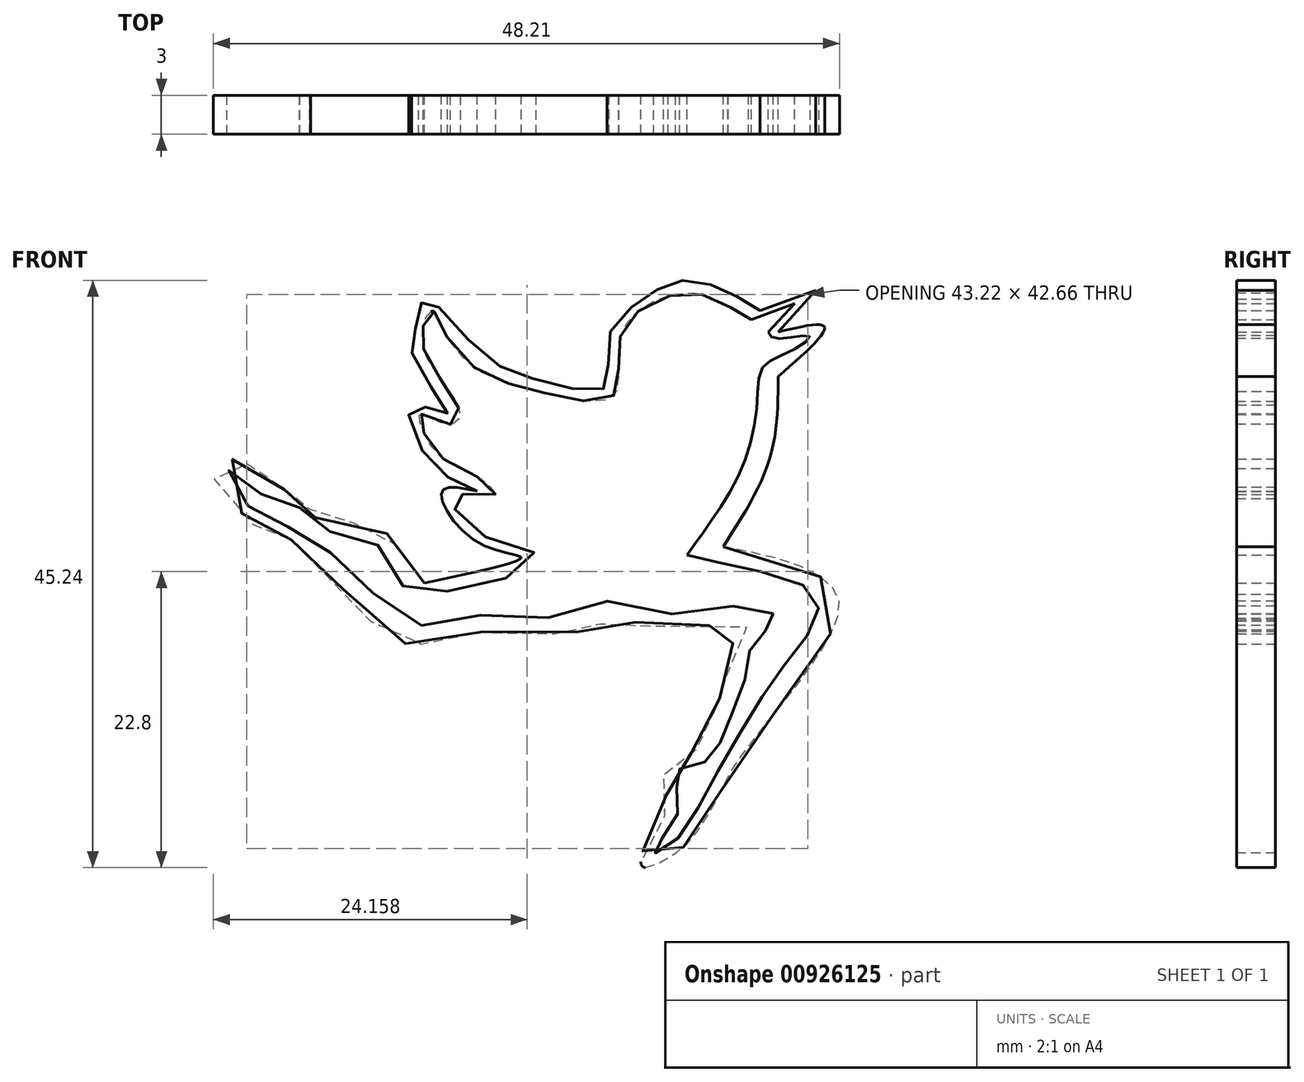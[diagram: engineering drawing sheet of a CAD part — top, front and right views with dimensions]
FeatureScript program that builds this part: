
annotation { "Feature Type Name" : "Feature", "Feature Type Description" : "" }
export const myFeature = defineFeature(function(context is Context, id is Id, definition is map)
    precondition{}
    {
        {
            var Q0;
            Q0=qCreatedBy(makeId("Front.planeOp"),FACE);
            var sketch = newSketch(context, id + "F0", { "sketchPlane" : qUnion([Q0])});
            skFitSpline(sketch, "E0", {"points": [v(20.55, 1.86) * mm, v(24.12, 8.6) * mm, v(24.78, 14.95) * mm], "startDerivative": vector(8.26, 12.82) * mm, "endDerivative": vector(0.08, 13.38) * mm});
            skFitSpline(sketch, "E1", {"points": [v(24.78, 14.95) * mm, v(28.35, 18.79) * mm, v(24.78, 18.39) * mm], "startDerivative": vector(10.47, 9.17) * mm, "endDerivative": vector(-11.15, -2.66) * mm});
            skLineSegment(sketch, "E2", {"start": v(24.78, 18.39) * mm, "end": v(27.67, 21.6) * mm});
            skLineSegment(sketch, "E3", {"start": v(27.67, 21.6) * mm, "end": v(23.38, 20.02) * mm});
            skFitSpline(sketch, "E4", {"points": [v(23.38, 20.02) * mm, v(20.68, 21.6) * mm, v(17.37, 22.35) * mm, v(14.44, 21) * mm, v(11.67, 17.84) * mm, v(11.51, 14.16) * mm, v(6.86, 14.54) * mm, v(1.82, 16.87) * mm, v(-2.38, 20.92) * mm, v(-3.13, 18.79) * mm, v(-3.2, 16.19) * mm, v(-0.73, 12.06) * mm, v(-3.36, 12.73) * mm, v(-2.3, 8.75) * mm, v(1.6, 6.12) * mm], "startDerivative": vector(-39.63, 25.99) * mm, "endDerivative": vector(52.94, -21.02) * mm});
            skFitSpline(sketch, "E5", {"points": [v(1.6, 6.12) * mm, v(-1.1, 6.12) * mm, v(1.6, 2.22) * mm, v(4.98, 1.01) * mm, v(-2.46, -0.94) * mm], "startDerivative": vector(-18.88, 4.2) * mm, "endDerivative": vector(-34.46, -7.28) * mm});
            skFitSpline(sketch, "E6", {"points": [v(-2.46, -0.94) * mm, v(-4.04, 1.01) * mm, v(-5.39, 2.9) * mm, v(-8.47, 3.72) * mm, v(-11.25, 4.4) * mm, v(-11.25, 5.45) * mm, v(-12.53, 6.12) * mm, v(-15, 6.87) * mm, v(-16.58, 8.53) * mm, v(-18.69, 7.63) * mm, v(-16.58, 4.47) * mm, v(-14.7, 2.97) * mm, v(-13.05, 2.6) * mm, v(-11.17, 0.64) * mm, v(-8.4, -1.77) * mm, v(-5.24, -5.15) * mm, v(-1.86, -5.52) * mm, v(2.2, -4.7) * mm, v(8.28, -4.85) * mm, v(10.46, -4.32) * mm, v(12.72, -3.8) * mm, v(15.8, -4.47) * mm, v(19.33, -4.24) * mm, v(22.48, -4.02) * mm, v(21.2, -5.75) * mm, v(20.9, -8.15) * mm, v(20.38, -9.58) * mm, v(19.47, -11.94) * mm, v(18.4, -13.85) * mm, v(16.29, -14.7) * mm, v(16.07, -16.74) * mm, v(16.22, -18.5) * mm, v(14.73, -20.77) * mm, v(14.38, -22.82) * mm, v(16.85, -21.76) * mm, v(18.4, -20.28) * mm, v(20.24, -17.24) * mm, v(21.45, -14.98) * mm, v(26.46, -8.47) * mm, v(29, -4.45) * mm, v(29.43, -2.18) * mm, v(27.24, 0) * mm, v(20.55, 1.86) * mm], "startDerivative": vector(-76.05, 84.18) * mm, "endDerivative": vector(-200.72, 39.21) * mm});
            skLineSegment(sketch, "E7", {"start": v(22.7, 19.34) * mm, "end": v(26.04, 20.57) * mm});
            skLineSegment(sketch, "E8", {"start": v(26.04, 20.57) * mm, "end": v(24, 18.39) * mm});
            skPoint(sketch, "E9.13.internal.snap0", {"position": v(25.02, 19.48) * mm});
            skFitSpline(sketch, "E9", {"points": [v(22.7, 19.34) * mm, v(21.48, 20.07) * mm, v(19.26, 21.17) * mm, v(16.67, 21.24) * mm, v(13.78, 19.82) * mm, v(12.56, 17.74) * mm, v(12.48, 15) * mm, v(11.98, 13.37) * mm, v(9.1, 13.17) * mm, v(5.2, 14.1) * mm, v(1.85, 15.35) * mm, v(-1.02, 18.52) * mm, v(-1.76, 20) * mm, v(-2.38, 19.48) * mm, v(-2.6, 18.02) * mm, v(-2.38, 16.6) * mm, v(-0.39, 13.6) * mm, v(0.25, 11.79) * mm, v(-0.73, 11.28) * mm, v(-2.85, 12.06) * mm, v(-2.65, 10.95) * mm, v(-1.17, 8.75) * mm, v(1.98, 7) * mm, v(3.02, 5.89) * mm], "startDerivative": vector(-32.65, 19.7) * mm, "endDerivative": vector(21.66, -32.08) * mm});
            skFitSpline(sketch, "E10", {"points": [v(3.02, 5.89) * mm, v(1.9, 5.53) * mm, v(0.54, 5.89) * mm, v(-0.37, 6.01) * mm, v(-0.48, 5.58) * mm, v(0.38, 3.97) * mm, v(1.6, 2.87) * mm, v(5.01, 1.8) * mm, v(6.1, 1.2) * mm, v(5.26, 0) * mm, v(1.34, -1.08) * mm, v(-1.85, -1.8) * mm, v(-3.92, -1.35) * mm, v(-5.56, 1.06) * mm, v(-6.52, 2.4) * mm, v(-9.83, 3.02) * mm, v(-12.08, 3.93) * mm, v(-12.19, 5.37) * mm, v(-14.74, 5.7) * mm, v(-16.4, 7.66) * mm, v(-17.65, 7.6) * mm, v(-17.08, 6.09) * mm, v(-14.9, 4.2) * mm, v(-13.11, 3.44) * mm, v(-10.95, 2.03) * mm, v(-8, 0.34) * mm, v(-5.3, -3.05) * mm, v(-1.86, -4.22) * mm, v(2.13, -3.39) * mm, v(7.2, -3.6) * mm, v(11.3, -2.35) * mm, v(15.91, -3.28) * mm, v(20.4, -2.8) * mm, v(23.1, -2.9) * mm, v(24.4, -3.3) * mm], "startDerivative": vector(-53.28, -25.96) * mm, "endDerivative": vector(54.39, -20.49) * mm});
            skFitSpline(sketch, "E11", {"points": [v(24.4, -3.3) * mm, v(24.04, -4.35) * mm, v(22.7, -5.87) * mm, v(22.11, -8.78) * mm, v(20.58, -12.44) * mm, v(19.53, -14.53) * mm, v(17.3, -15.2) * mm, v(16.86, -16.11) * mm, v(17.15, -18.29) * mm, v(15.8, -20.65) * mm, v(15.2, -21.72) * mm, v(16.74, -20.9) * mm, v(19.24, -17.07) * mm, v(22.42, -11.55) * mm, v(25.32, -7.17) * mm, v(27.66, -3.87) * mm, v(27.4, -1.63) * mm, v(21.63, 0.33) * mm, v(17.76, 1.22) * mm], "startDerivative": vector(-5.18, -31.06) * mm, "endDerivative": vector(-52.1, 12.79) * mm});
            skFitSpline(sketch, "E12", {"points": [v(17.76, 1.22) * mm, v(19.6, 3.8) * mm, v(22.02, 7.96) * mm, v(23.13, 12.73) * mm, v(23.58, 15.66) * mm, v(25.46, 16.77) * mm, v(27.22, 17.99) * mm, v(26.27, 18.05) * mm, v(24.4, 17.92) * mm, v(24, 18.39) * mm], "startDerivative": vector(13.75, 19.08) * mm, "endDerivative": vector(-4.76, 10.16) * mm});
            skSolve(sketch);
        }
        {
            var Q0;
            Q0 = qSketchRegion(id + "F0", true);
            extrude(context, id + "F1", {"entities" : qUnion([Q0]), "depth" : 3 * mm, "offsetDistance" : 25.4 * mm});
        }
    });
